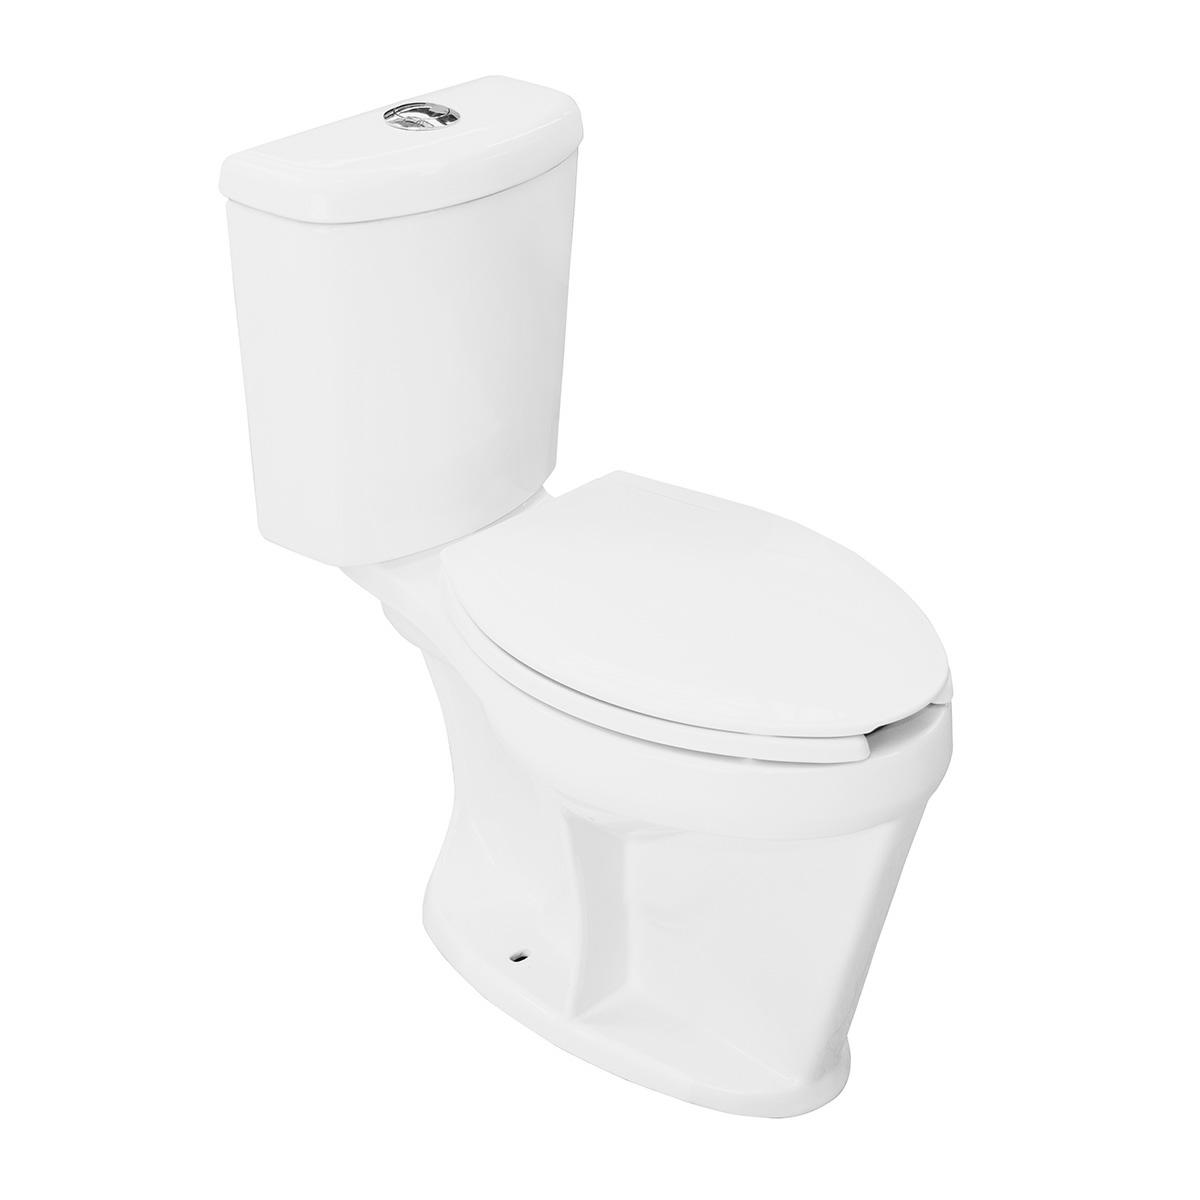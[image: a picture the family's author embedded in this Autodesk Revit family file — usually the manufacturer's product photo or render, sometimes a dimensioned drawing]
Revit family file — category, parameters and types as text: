
# Revit family: WC 2.5
name_source: partatom
category: Aparatos sanitarios
units: mm (PartAtom-declared; Revit-internal decimal feet)

## family parameters
Compartido = No
Corte con vacíos al cargar = No
Cota de conector redondo = Diámetro de uso
Número OmniClass = 23.45.00.00
Punto de cálculo de habitación = No
Se basa en plano de trabajo = No
Siempre vertical = Sí
Tipo de pieza = Normal
Título OmniClass = Sanitary, Laundry, and Cleaning Equipment

## types (1)
- WC 2.5
    Comentarios de tipo = Ceramic
    Data Sheet = https://www.helvex.com.mx
    Descripción = Inodoro, Taza y Tanque WC 2.5 Altura Confortable, Sistema Turvex
    Elevación por defecto = 0"
    Fabricante = HELVEX
    High Gloss Ceramic = High Gloss Ceramic
    Imagen de tipo = WC 2.5.jpg
    Inlet Threads = Feeding: Ø15/16" - 14 NS - 1;  Flush: Couple With Sanitary Flange
    Instructive = https://www.helvex.com.mx
    Max. Working Pressure = 85.3 psi
    Maximum Consumption = 0.66 gpf
    Min. Working Pressure = 3.6 psi
    Modelo = WC 2.5
    Total Height = 32"
    Total Length = 26"
    Total Width = 14"
    URL = https://www.helvex.com.mx

## geometry (parser evidence)
native form markers: Sweep x3
no freeform markers — native parametric forms only
